# Revit family: PRD_FrankeWS_WtrSpplFttngsFrWshBsnsAndTrghs_ElectronicPillarMixer_F3EM1001-1009
name_source: partatom
category: Plumbing Fixtures
revit_build: Autodesk Revit 2018 (Build: 20190510_1515(x64)
units: mm (PartAtom-declared; Revit-internal decimal feet)

## family parameters
Always vertical = No
Cut with Voids When Loaded = No
OmniClass Number = 23.45.55.14
OmniClass Title = Single Faucets
Part Type = Normal
Room Calculation Point = No
Round Connector Dimension = Use Diameter
Shared = No
Work Plane-Based = Yes

## types (8) — shared parameters
AssetType = Fixed
Category = Pr_40_20_87_98, Washbasin taps
Color = Chrome
Default Elevation = 750 mm  [stored 2.46063 ft]
DefaultAutomaticHygieneFlushing = 24H-AFTER-ACTIVITY
Depressurised = no
DiameterNominal = 15.00 mm
DurationUnit = year
FaucetFunction = MIXED
FaucetMaterial = PRD_AR_ChromatedBrass_HighPolished
FaucetOperation = ELECTRONIC
FaucetType = PILLAR
Finish = high-polished chromium-plated brass
FlowColdWater = 0.1 L/s
FlowHotWater = 0.1 L/s
Form = Self-closing
FunctionalPrinciple = ELECTRONIX-C
HygieneFlushing = yes
IfcExportAs = IfcValveType
IfcExportType = FAUCET
IntegralAccessories = Extension cable ACEX9010, 2-pin, length 5 m.
Manufacturer = KWC Group AG
ManufacturerName = KWC Group AG
ManufacturerURL = www.kwc.com
Material = Brass
MaterialsBody = Brass
MaterialsFinishAndColour = high-polished chromium-plated brass
MinimumFlowPressure = 1.00 bar
NBSDescription = Water supply fittings for wash basins and troughs
NBSReference = 45-35-70/371
OutletMaterial = PRD_AR_SyntheticGrey
PositionOfPowerConnection = BOTTOM
PowerConsumption = 1.5
ProductInformation = https://pim.kwc.com
ProtectiveShutdown = yes
ScrewMaterial = PRD_AR_ChromatedBrass_HighPolished
SensorMaterial = PRD_AR_SyntheticDarkGrey
SoundInsulation = no
SpoutProjection = 100.00 mm
ThermalDisinfection = no
TypeOfMixing = yes
TypeOfMounting = TAPHOLE
TypeOfOperation = SENSOR-OPERATION
TypeOfSensor = OPTO-ELEC-SENSOR
TypeOfTap = PILLAR-TAB
URL = www.kwc.com
Uniclass2015Code = Pr_40_20_87_98
Uniclass2015Title = Washbasin taps
Uniclass2015Version = Products v1.10
Version = 1
WarrantyDurationUnit = year
zero-valued in all types: NominalHeight, NominalLength, NominalWidth

## per-type parameters (varying)
| type | BIMObjectName | Description | GrossWeight | Model | ModelNumber | ModelReference | Name | NetWeight | PowerSupplyConnection | ProtectiveSystemIP | VolumeFlowRate |
| F3EM1001 - 0.10 L/s with 6 V lithium battery | PRD_AR_WtrSplyFtngsForWshBsnsAndTrghs_ElectronicPillarMixer_F3EM1001 | F3E-Mix pillar mixer DN 15 for sanitary facilities, opto-electronically controlled. For connection to hot and cold water via hoses with integrated backflow preventer and strainers. Control electronics, solenoid valve cartridge and sensor in all-metal housing, high-polished chromium-plated brass, with temperature lever and adjustable, turn-proof temperature stop. Aerator with integrated flow regulator 6.0 l/min. Activated water hygiene flushing 24 hours after last activation, safety switch-off with continuous reflection and saving of statistical data. With option for parameterization and communication via optional, bidirectional remote control. With battery compartment including 6 V lithium battery (CR-P2) for installation under the washbasin. | 1.47 kg | F3EM1001 | 2030033388 | F3EM1001 | F3 electronic pillar mixer F3EM1001 | 1.40 kg | BATTERY-6-V | tap IP59K | 0.10 L/s at 3 bar |
| F3EM1002 - 0.10 L/s with 100 - 240 V AC plug-in power supply unit | PRD_AR_WtrSplyFtngsForWshBsnsAndTrghs_ElectronicPillarMixer_F3EM1002 | F3E-Mix pillar mixer DN 15 for sanitary facilities, opto-electronically controlled. For connection to hot and cold water via hoses with integrated backflow preventer and strainers. Control electronics, solenoid valve cartridge and sensor in all-metal housing, high-polished chromium-plated brass, with temperature lever and adjustable, turn-proof temperature stop. Aerator with integrated flow regulator 6.0 l/min. Activated water hygiene flushing 24 hours after last activation, safety switch-off with continuous reflection and saving of statistical data. With option for parameterization and communication via optional, bidirectional remote control. With 100 -240 V AC plug-in power supply unit. | 1.50 kg | F3EM1002 | 2030033389 | F3EM1002 | F3 electronic pillar mixer F3EM1002 | 1.42 kg | 100-240VAC | tap IP59K | 0.10 L/s at 3 bar |
| F3EM1003 - 0.10 L/s with in-wall power supply 100 - 240 V AC | PRD_AR_WtrSplyFtngsForWshBsnsAndTrghs_ElectronicPillarMixer_F3EM1003 | F3E-Mix pillar mixer DN 15 for sanitary facilities, opto-electronically controlled. For connection to hot and cold water via hoses with integrated backflow preventer and strainers. Control electronics, solenoid valve cartridge and sensor in all-metal housing, high-polished chromium-plated brass, with temperature lever and adjustable, turn-proof temperature stop. Aerator with integrated flow regulator 6.0 l/min. Activated water hygiene flushing 24 hours after last activation, safety switch-off with continuous reflection and saving of statistical data. With option for parameterization and communication via optional, bidirectional remote control. With in-wall power supply 100 - 240 V AC. | 1.50 kg | F3EM1003 | 2030033545 | F3EM1003 | F3 electronic pillar mixer F3EM1003 | 1.43 kg | 100-240VAC | tap IP59K | 0.10 L/s at 3 bar |
| F3EM1005 - 0.10 L/s with separate power supply via power supply unit 6.75 V / 12 V DC | PRD_AR_WtrSplyFtngsForWshBsnsAndTrghs_ElectronicPillarMixer_F3EM1005 | F3E-Mix pillar mixer DN 15 for sanitary facilities, opto-electronically controlled. For connection to hot and cold water via hoses with integrated backflow preventer and strainers. Control electronics, solenoid valve cartridge and sensor in all-metal housing, high-polished chromium-plated brass, with temperature lever and adjustable, turn-proof temperature stop. Aerator with integrated flow regulator 6.0 l/min. Activated water hygiene flushing 24 hours after last activation, safety switch-off with continuous reflection and saving of statistical data. With option for parameterization and communication via optional, bidirectional remote control. Separate power supply via power supply unit 6.75 V / 12 V DC. | 1.40 kg | F3EM1005 | 2030039469 | F3EM1005 | F3 electronic pillar mixer F3EM1005 | 1.33 kg | 6-12-VDC | IP59K | 0.10 L/s at 3 bar |
| F3EM1006 - 0.05 L/s with 6 V lithium battery | PRD_AR_WtrSplyFtngsForWshBsnsAndTrghs_ElectronicPillarMixer_F3EM1006 | F3E-Mix pillar mixer DN 15 for sanitary facilities, opto-electronically controlled. For connection to hot and cold water via hoses with integrated backflow preventer and strainers. Control electronics, solenoid valve cartridge and sensor in all-metal housing, highpolished chromium-plated brass, with temperature lever and adjustable, turn-proof temperature stop. Aerator with integrated flow regulator 3.0 l/min. Activated water hygiene flushing 24 hours after last activation, safety switch-off with continuous reflection and saving of statistical data. With option for parameterization and communication via optional, bidirectional remote control. With battery compartment including 6 V lithium battery (CR-P2) for installation under the washbasin. | 1.44 kg | F3EM1006 | 2030039470 | F3EM1006 | F3 electronic pillar mixer F3EM1006 | 1.40 kg | BATTERY-6-V | tap IP59K | 0.05 L/s at 3 bar |
| F3EM1007 - 0.05 L/s with 100 - 240 V AC plug-in power supply unit | PRD_AR_WtrSplyFtngsForWshBsnsAndTrghs_ElectronicPillarMixer_F3EM1007 | F3E-Mix pillar mixer DN 15 for sanitary facilities, opto-electronically controlled. For connection to hot and cold water via hoses with integrated backflow preventer and strainers. Control electronics, solenoid valve cartridge and sensor in all-metal housing, highpolished chromium-plated brass, with temperature lever and adjustable, turn-proof temperature stop. Aerator with integrated flow regulator 3.0 l/min. Activated water hygiene flushing 24 hours after last activation, safety switch-off with continuous reflection and saving of statistical data. With option for parameterization and communication via optional, bidirectional remote control. With 100 - 240 V AC plug-in power supply unit. | 1.40 kg | F3EM1007 | 2030039471 | F3EM1007 | F3 electronic pillar mixer F3EM1007 | 1.33 kg | 100-240VAC | tap IP59K | 0.05 L/s at 3 bar |
| F3EM1008 - 0.05 L/s with in-wall power supply 100 - 240 V AC | PRD_AR_WtrSplyFtngsForWshBsnsAndTrghs_ElectronicPillarMixer_F3EM1008 | F3E-Mix pillar mixer DN 15 for sanitary facilities, opto-electronically controlled. For connection to hot and cold water via hoses with integrated backflow preventer and strainers. Control electronics, solenoid valve cartridge and sensor in all-metal housing, highpolished chromium-plated brass, with temperature lever and adjustable, turn-proof temperature stop. Aerator with integrated flow regulator 3.0 l/min. Activated water hygiene flushing 24 hours after last activation, safety switch-off with continuous reflection and saving of statistical data. With option for parameterization and communication via optional, bidirectional remote control. With in-wall power supply 100 - 240 V AC. | 1.40 kg | F3EM1008 | 2030039472 | F3EM1008 | F3 electronic pillar mixer F3EM1008 | 1.33 kg | 100-240VAC | tap IP59K | 0.05 L/s at 3 bar |
| F3EM1009 - 0.05 L/s with separate power supply via power supply unit 6.75 V / 12 V DC | PRD_AR_WtrSplyFtngsForWshBsnsAndTrghs_ElectronicPillarMixer_F3EM1009 | F3E-Mix pillar mixer DN 15 for sanitary facilities, opto-electronically controlled. For connection to hot and cold water via hoses with integrated backflow preventer and strainers. Control electronics, solenoid valve cartridge and sensor in all-metal housing, highpolished chromium-plated brass, with temperature lever and adjustable, turn-proof temperature stop. Aerator with integrated flow regulator 3.0 l/min. Activated water hygiene flushing 24 hours after last activation, safety switch-off with continuous reflection and saving of statistical data. With option for parameterization and communication via optional, bidirectional remote control. Separate power supply via power supply unit 6.75 V / 12 V DC. | 1.40 kg | F3EM1009 | 2030039473 | F3EM1009 | F3 electronic pillar mixer F3EM1009 | 1.33 kg | 6-12-VDC | IP59K | 0.05 L/s at 3 bar |

note: [stored X ft] marks values corroborated as IEEE doubles in the binary element streams (Revit-internal decimal feet)

## geometry (parser evidence)
native form markers: Sweep x2
no freeform markers — native parametric forms only
